# Revit family: S-865
name_source: partatom
category: Uniones de tubería
revit_build: Autodesk Revit 2015 (Build: 20140606_1530(x64)
units: mm (PartAtom-declared; Revit-internal decimal feet)

## types (2) — shared parameters
Amax = 220 mm  [stored 0.721785 ft]
Amin = 150 mm
Caudal = 0.4 L/s
Certificados = http://www.jimten.com
Comentarios de tipo = FACIL INSTALACION GRACIAS A SU SISTEMA DE JUNTAS INTEGRADAS, TAPON DE REGISTRO INFERIOR
Descripción = SIFON BOTELLA JUNTAFIX, SALIDA HORIZONTAL, RACOR EXTENSIBLE CON TOPE INFERIOR, JUNTAFIX
Fabricante = Jimten
Material = PP (Blanco)
Modelo = S-865
URL = http://www.jimten.com

## per-type parameters (varying)
| type | Aplicación | De | Ds | Entradas | Referencia | Salida |
| S-865_1 1/2" | FREGADERO, LAVABO, BIDET | 38 mm | 40 mm  [stored 0.131234 ft] | 1 1/2" ROSCA HEMBRA | 001658 | Ø40 MM (HEMBRA) |
| S-865_1 1/4" | LAVABO, BIDET | 32 mm  [stored 0.104987 ft] | 32 mm  [stored 0.104987 ft] | 1 1/4" ROSCA HEMBRA | 001659 | Ø32 MM (HEMBRA) |

note: [stored X ft] marks values corroborated as IEEE doubles in the binary element streams (Revit-internal decimal feet)

## geometry (parser evidence)
native form markers: Blend x3
no freeform markers — native parametric forms only
